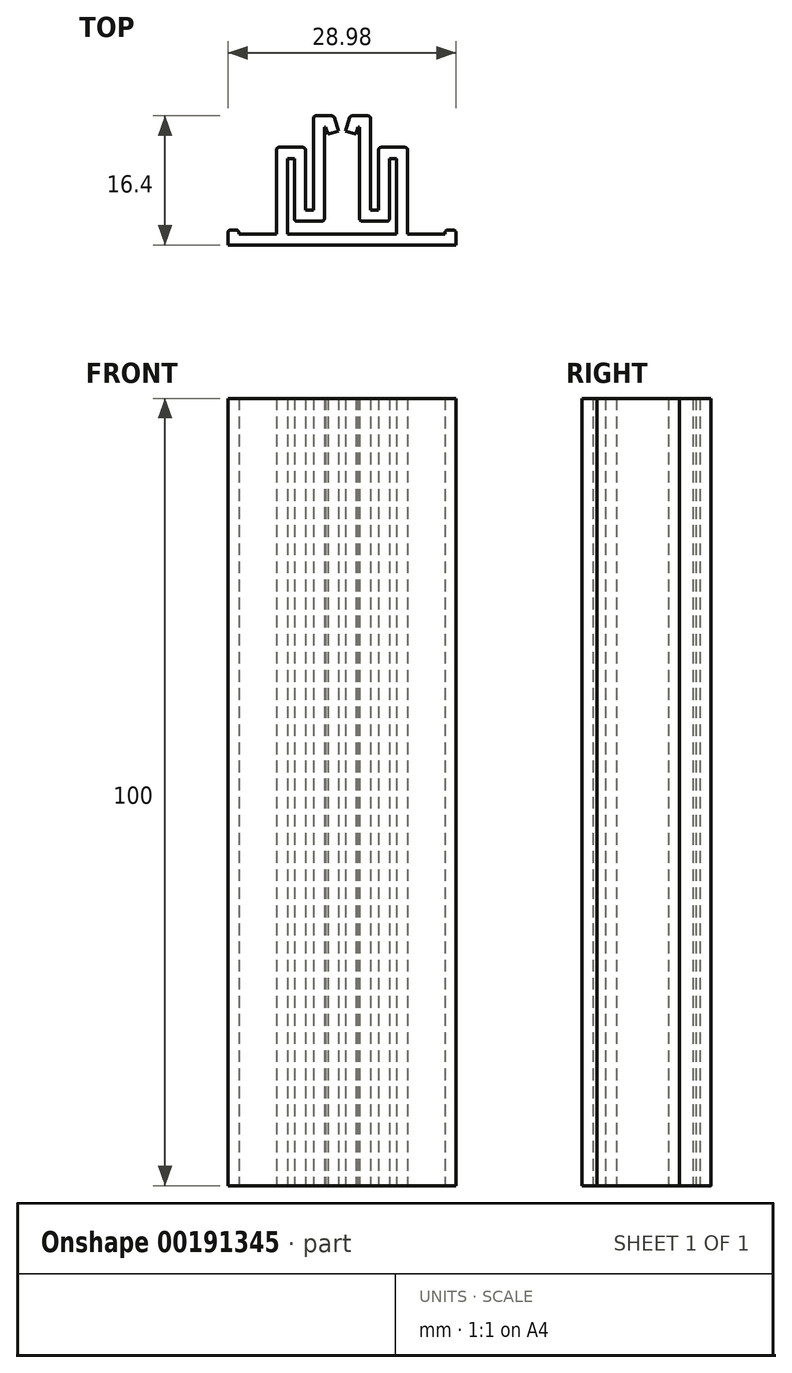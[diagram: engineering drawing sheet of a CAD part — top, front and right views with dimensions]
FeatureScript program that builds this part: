
annotation { "Feature Type Name" : "Feature", "Feature Type Description" : "" }
export const myFeature = defineFeature(function(context is Context, id is Id, definition is map)
    precondition{}
    {
        {
            var Q0;
            Q0=qCreatedBy(makeId("Top.planeOp"),FACE);
            var sketch = newSketch(context, id + "F0", { "sketchPlane" : qUnion([Q0])});
            skLineSegment(sketch, "E0", {"start": v(0.44, 14.91) * mm, "end": v(1.04, 16.82) * mm});
            skLineSegment(sketch, "E1", {"start": v(1.04, 16.82) * mm, "end": v(3.64, 16.82) * mm});
            skLineSegment(sketch, "E2", {"start": v(3.64, 16.82) * mm, "end": v(3.64, 4.82) * mm});
            skLineSegment(sketch, "E3", {"start": v(3.64, 4.82) * mm, "end": v(4.64, 4.82) * mm});
            skLineSegment(sketch, "E4", {"start": v(4.64, 4.82) * mm, "end": v(4.64, 12.82) * mm});
            skLineSegment(sketch, "E5", {"start": v(4.64, 12.82) * mm, "end": v(8.34, 12.82) * mm});
            skLineSegment(sketch, "E6", {"start": v(8.34, 12.82) * mm, "end": v(8.34, 1.82) * mm});
            skLineSegment(sketch, "E7", {"start": v(8.34, 1.82) * mm, "end": v(13.1, 1.82) * mm});
            skLineSegment(sketch, "E8", {"start": v(13.1, 1.82) * mm, "end": v(13.1, 2.32) * mm});
            skLineSegment(sketch, "E9.0", {"start": v(14.5, 0.42) * mm, "end": v(14.5, 2.32) * mm});
            skLineSegment(sketch, "E9.1", {"start": v(6.94, 0.42) * mm, "end": v(14.5, 0.42) * mm});
            skLineSegment(sketch, "E9.2", {"start": v(6.94, 11.42) * mm, "end": v(6.94, 1.82) * mm});
            skLineSegment(sketch, "E9.3", {"start": v(6.04, 11.42) * mm, "end": v(6.94, 11.42) * mm});
            skLineSegment(sketch, "E9.4", {"start": v(6.04, 3.42) * mm, "end": v(6.04, 11.42) * mm});
            skLineSegment(sketch, "E9.5", {"start": v(1.78, 14.52) * mm, "end": v(2.07, 15.42) * mm});
            skLineSegment(sketch, "E9.6", {"start": v(2.07, 15.42) * mm, "end": v(2.24, 15.42) * mm});
            skLineSegment(sketch, "E9.7", {"start": v(2.24, 15.42) * mm, "end": v(2.24, 3.42) * mm});
            skLineSegment(sketch, "E9.8", {"start": v(2.24, 3.42) * mm, "end": v(6.04, 3.42) * mm});
            skLineSegment(sketch, "E10", {"start": v(0.44, 14.91) * mm, "end": v(1.78, 14.52) * mm});
            skLineSegment(sketch, "E11", {"start": v(13.1, 2.32) * mm, "end": v(14.5, 2.32) * mm});
            skLineSegment(sketch, "E12.MirrorCS", {"start": v(-13.1, 2.32) * mm, "end": v(-14.5, 2.32) * mm});
            skLineSegment(sketch, "E13.MirrorCS", {"start": v(-6.04, 3.42) * mm, "end": v(-6.04, 11.42) * mm});
            skLineSegment(sketch, "E14.MirrorCS", {"start": v(-1.78, 14.52) * mm, "end": v(-2.07, 15.42) * mm});
            skLineSegment(sketch, "E15.MirrorCS", {"start": v(-2.07, 15.42) * mm, "end": v(-2.24, 15.42) * mm});
            skLineSegment(sketch, "E16.MirrorCS", {"start": v(-0.44, 14.91) * mm, "end": v(-1.04, 16.82) * mm});
            skLineSegment(sketch, "E17.MirrorCS", {"start": v(-1.04, 16.82) * mm, "end": v(-3.64, 16.82) * mm});
            skLineSegment(sketch, "E18.MirrorCS", {"start": v(-3.64, 16.82) * mm, "end": v(-3.64, 4.82) * mm});
            skLineSegment(sketch, "E19.MirrorCS", {"start": v(-3.64, 4.82) * mm, "end": v(-4.64, 4.82) * mm});
            skLineSegment(sketch, "E20.MirrorCS", {"start": v(-4.64, 4.82) * mm, "end": v(-4.64, 12.82) * mm});
            skLineSegment(sketch, "E21.MirrorCS", {"start": v(-4.64, 12.82) * mm, "end": v(-8.34, 12.82) * mm});
            skLineSegment(sketch, "E22.MirrorCS", {"start": v(-8.34, 12.82) * mm, "end": v(-8.34, 1.82) * mm});
            skLineSegment(sketch, "E23.MirrorCS", {"start": v(-8.34, 1.82) * mm, "end": v(-13.1, 1.82) * mm});
            skLineSegment(sketch, "E24.MirrorCS", {"start": v(-13.1, 1.82) * mm, "end": v(-13.1, 2.32) * mm});
            skLineSegment(sketch, "E25.MirrorCS", {"start": v(-14.5, 0.42) * mm, "end": v(-14.5, 2.32) * mm});
            skLineSegment(sketch, "E26.MirrorCS", {"start": v(-6.94, 0.42) * mm, "end": v(-14.5, 0.42) * mm});
            skLineSegment(sketch, "E27.MirrorCS", {"start": v(-6.94, 11.42) * mm, "end": v(-6.94, 1.82) * mm});
            skLineSegment(sketch, "E28.MirrorCS", {"start": v(-6.04, 11.42) * mm, "end": v(-6.94, 11.42) * mm});
            skLineSegment(sketch, "E29.MirrorCS", {"start": v(-0.44, 14.91) * mm, "end": v(-1.78, 14.52) * mm});
            skLineSegment(sketch, "E30.MirrorCS", {"start": v(-2.24, 15.42) * mm, "end": v(-2.24, 3.42) * mm});
            skLineSegment(sketch, "E31.MirrorCS", {"start": v(-2.24, 3.42) * mm, "end": v(-6.04, 3.42) * mm});
            skLineSegment(sketch, "E32", {"start": v(-6.94, 0.42) * mm, "end": v(6.94, 0.42) * mm});
            skLineSegment(sketch, "E33", {"start": v(-6.94, 1.82) * mm, "end": v(6.94, 1.82) * mm});
            skSolve(sketch);
        }
        {
            var Q0;
            Q0=makeQuery(id+"F0.imprint","IMPRINT",FACE,{"disambiguationData":[TD([[makeQuery(id+"F0.imprint","IMPRINT",EDGE,{"derivedFrom":sQuery(id+"F0.wireOp",EDGE,"E0")}),-1.0]])]});
            extrude(context, id + "F1", {"entities" : qUnion([Q0]), "depth" : 100 * mm, "symmetric" : true});
        }
        {
            var Q0;
            Q0=makeQuery(id+"F1.opExtrude","SWEPT_EDGE",EDGE,{"disambiguationData":[OSD([sQuery(id+"F0.wireOp",EDGE,"E9.0"),sQuery(id+"F0.wireOp",EDGE,"E11")])]});
            fillet(context, id + "F2", {"entities" : qUnion([Q0]), "radius" : .35 * mm, "tangentPropagation" : true, "allowEdgeOverflow" : false});
        }
        {
            var Q0;
            Q0=makeQuery(id+"F1.opExtrude","SWEPT_EDGE",EDGE,{"disambiguationData":[OSD([sQuery(id+"F0.wireOp",EDGE,"E8"),sQuery(id+"F0.wireOp",EDGE,"E11")])]});
            var Q1;
            Q1=makeQuery(id+"F1.opExtrude","SWEPT_EDGE",EDGE,{"disambiguationData":[OSD([sQuery(id+"F0.wireOp",EDGE,"E5"),sQuery(id+"F0.wireOp",EDGE,"E6")])]});
            var Q2;
            Q2=makeQuery(id+"F1.opExtrude","SWEPT_EDGE",EDGE,{"disambiguationData":[OSD([sQuery(id+"F0.wireOp",EDGE,"E4"),sQuery(id+"F0.wireOp",EDGE,"E5")])]});
            var Q3;
            Q3=makeQuery(id+"F1.opExtrude","SWEPT_EDGE",EDGE,{"disambiguationData":[OSD([sQuery(id+"F0.wireOp",EDGE,"E1"),sQuery(id+"F0.wireOp",EDGE,"E2")])]});
            var Q4;
            Q4=makeQuery(id+"F1.opExtrude","SWEPT_EDGE",EDGE,{"disambiguationData":[OSD([sQuery(id+"F0.wireOp",EDGE,"E0"),sQuery(id+"F0.wireOp",EDGE,"E1")])]});
            fillet(context, id + "F3", {"entities" : qUnion([Q0, Q1, Q2, Q3, Q4]), "radius" : .35 * mm, "tangentPropagation" : true, "allowEdgeOverflow" : false});
        }
        {
            var Q0;
            Q0=makeQuery(id+"F1.opExtrude","SWEPT_EDGE",EDGE,{"disambiguationData":[OSD([sQuery(id+"F0.wireOp",EDGE,"E9.4"),sQuery(id+"F0.wireOp",EDGE,"E9.8")])]});
            var Q1;
            Q1=makeQuery(id+"F1.opExtrude","SWEPT_EDGE",EDGE,{"disambiguationData":[OSD([sQuery(id+"F0.wireOp",EDGE,"E9.7"),sQuery(id+"F0.wireOp",EDGE,"E9.8")])]});
            var Q2;
            Q2=makeQuery(id+"F1.opExtrude","SWEPT_EDGE",EDGE,{"disambiguationData":[OSD([sQuery(id+"F0.wireOp",EDGE,"E30.MirrorCS"),sQuery(id+"F0.wireOp",EDGE,"E31.MirrorCS")])]});
            fillet(context, id + "F4", {"entities" : qUnion([Q0, Q1, Q2]), "radius" : .35 * mm, "tangentPropagation" : true, "allowEdgeOverflow" : false});
        }
        {
            var Q0;
            Q0=makeQuery(id+"F1.opExtrude","SWEPT_EDGE",EDGE,{"disambiguationData":[OSD([sQuery(id+"F0.wireOp",EDGE,"E13.MirrorCS"),sQuery(id+"F0.wireOp",EDGE,"E31.MirrorCS")])]});
            var Q1;
            Q1=makeQuery(id+"F1.opExtrude","SWEPT_EDGE",EDGE,{"disambiguationData":[OSD([sQuery(id+"F0.wireOp",EDGE,"E21.MirrorCS"),sQuery(id+"F0.wireOp",EDGE,"E22.MirrorCS")])]});
            var Q2;
            Q2=makeQuery(id+"F1.opExtrude","SWEPT_EDGE",EDGE,{"disambiguationData":[OSD([sQuery(id+"F0.wireOp",EDGE,"E12.MirrorCS"),sQuery(id+"F0.wireOp",EDGE,"E25.MirrorCS")])]});
            var Q3;
            Q3=makeQuery(id+"F1.opExtrude","SWEPT_EDGE",EDGE,{"disambiguationData":[OSD([sQuery(id+"F0.wireOp",EDGE,"E17.MirrorCS"),sQuery(id+"F0.wireOp",EDGE,"E18.MirrorCS")])]});
            var Q4;
            Q4=makeQuery(id+"F1.opExtrude","SWEPT_EDGE",EDGE,{"disambiguationData":[OSD([sQuery(id+"F0.wireOp",EDGE,"E16.MirrorCS"),sQuery(id+"F0.wireOp",EDGE,"E17.MirrorCS")])]});
            var Q5;
            Q5=makeQuery(id+"F1.opExtrude","SWEPT_EDGE",EDGE,{"disambiguationData":[OSD([sQuery(id+"F0.wireOp",EDGE,"E20.MirrorCS"),sQuery(id+"F0.wireOp",EDGE,"E21.MirrorCS")])]});
            var Q6;
            Q6=makeQuery(id+"F1.opExtrude","SWEPT_EDGE",EDGE,{"disambiguationData":[OSD([sQuery(id+"F0.wireOp",EDGE,"E12.MirrorCS"),sQuery(id+"F0.wireOp",EDGE,"E24.MirrorCS")])]});
            fillet(context, id + "F5", {"entities" : qUnion([Q0, Q1, Q2, Q3, Q4, Q5, Q6]), "radius" : .35 * mm, "tangentPropagation" : true, "allowEdgeOverflow" : false});
        }
    });
